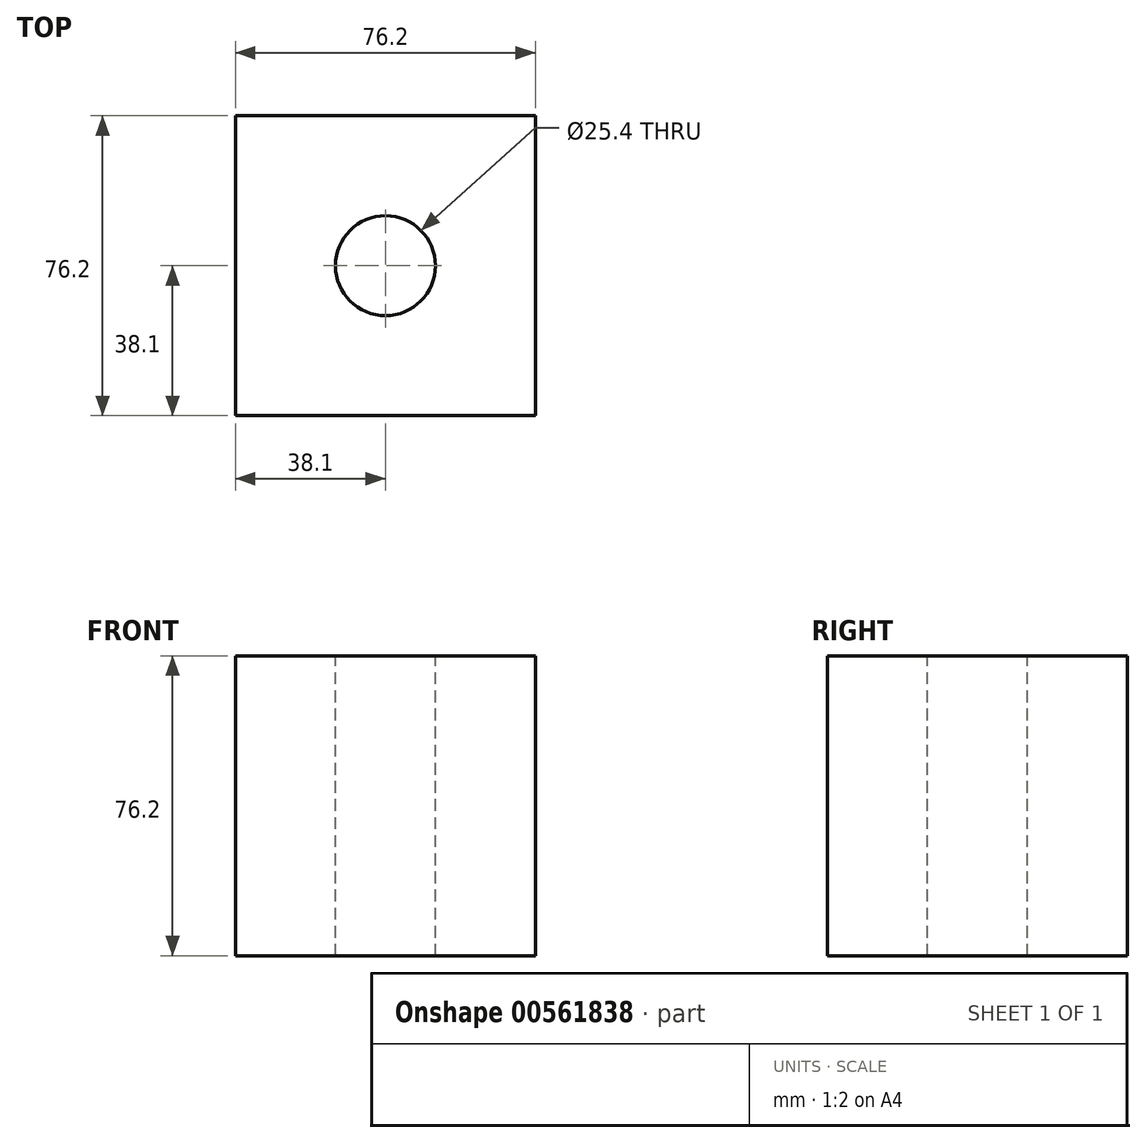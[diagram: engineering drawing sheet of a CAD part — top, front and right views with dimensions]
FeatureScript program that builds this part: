
annotation { "Feature Type Name" : "Feature", "Feature Type Description" : "" }
export const myFeature = defineFeature(function(context is Context, id is Id, definition is map)
    precondition{}
    {
        {
            var Q0;
            Q0=qCreatedBy(makeId("Front.planeOp"),FACE);
            var sketch = newSketch(context, id + "F0", { "sketchPlane" : qUnion([Q0])});
            skLineSegment(sketch, "E0.bottom", {"start": v(-49.95, -38.87) * mm, "end": v(26.25, -38.87) * mm});
            skLineSegment(sketch, "E0.top", {"start": v(-49.95, 37.33) * mm, "end": v(26.25, 37.33) * mm});
            skLineSegment(sketch, "E0.left", {"start": v(-49.95, -38.87) * mm, "end": v(-49.95, 37.33) * mm});
            skLineSegment(sketch, "E0.right", {"start": v(26.25, -38.87) * mm, "end": v(26.25, 37.33) * mm});
            skSolve(sketch);
        }
        {
            var Q0;
            Q0 = qSketchRegion(id + "F0", true);
            extrude(context, id + "F1", {"entities" : qUnion([Q0]), "oppositeDirection" : true, "depth" : 76.2 * mm, "offsetDistance" : 25.4 * mm});
        }
        {
            var Q0;
            Q0=makeQuery(id+"F1.opExtrude","SWEPT_FACE",FACE,{"disambiguationData":[OSD([sQuery(id+"F0.wireOp",EDGE,"E0.top")])]});
            var sketch = newSketch(context, id + "F2", { "sketchPlane" : qUnion([Q0])});
            skPoint(sketch, "E1", {"position": v(-11.85, 38.1) * mm});
            skSolve(sketch);
        }
        {
            var Q0;
            Q0=sQuery(id+"F2.wireOp",VERTEX,"E1");
            var Q1;
            Q1=makeQuery(id+"F1.opExtrude","SWEPT_BODY",BODY,{"disambiguationData":[OSD([sQuery(id+"F0.wireOp",EDGE,"E0.bottom"),sQuery(id+"F0.wireOp",EDGE,"E0.top"),sQuery(id+"F0.wireOp",EDGE,"E0.left"),sQuery(id+"F0.wireOp",EDGE,"E0.right")])]});
            hole(context, id + "F3", {"style" : HoleStyle.SIMPLE, "endStyle" : HoleEndStyle.THROUGH, "holeDiameter" : 25.4 * mm, "isTappedThrough" : true, "tappedDepth" : 12.7 * mm, "tapClearance" : 3, "locations" : qUnion([Q0]), "scope" : qUnion([Q1])});
        }
    });
